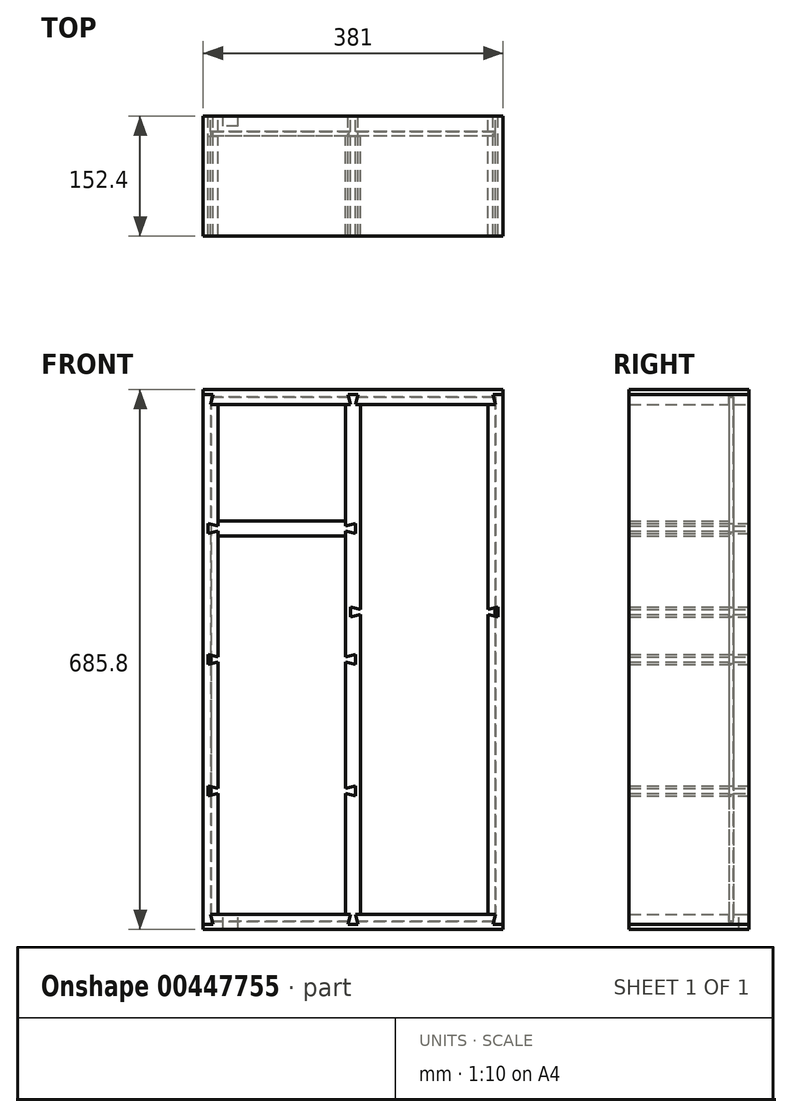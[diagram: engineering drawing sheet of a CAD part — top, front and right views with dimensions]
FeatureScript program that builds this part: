
annotation { "Feature Type Name" : "Feature", "Feature Type Description" : "" }
export const myFeature = defineFeature(function(context is Context, id is Id, definition is map)
    precondition{}
    {
        {
            var Q0;
            Q0=qCreatedBy(makeId("Front.planeOp"),FACE);
            var sketch = newSketch(context, id + "F0", { "sketchPlane" : qUnion([Q0])});
            skLineSegment(sketch, "E0.bottom", {"start": v(190.5, 342.9) * mm, "end": v(-190.5, 342.9) * mm});
            skLineSegment(sketch, "E0.top", {"start": v(190.5, -342.9) * mm, "end": v(-190.5, -342.9) * mm});
            skLineSegment(sketch, "E0.left", {"start": v(190.5, 342.9) * mm, "end": v(190.5, -342.9) * mm});
            skLineSegment(sketch, "E0.right", {"start": v(-190.5, 342.9) * mm, "end": v(-190.5, -342.9) * mm});
            skPoint(sketch, "E0.middle", {"position": v(0, 0) * mm});
            skLineSegment(sketch, "E1.0", {"start": v(-171.45, 323.85) * mm, "end": v(-171.45, -323.85) * mm});
            skLineSegment(sketch, "E1.1", {"start": v(190.5, 323.85) * mm, "end": v(-190.5, 323.85) * mm});
            skLineSegment(sketch, "E1.2", {"start": v(171.45, 323.85) * mm, "end": v(171.45, -323.85) * mm});
            skLineSegment(sketch, "E1.3", {"start": v(190.5, -323.85) * mm, "end": v(-190.5, -323.85) * mm});
            skLineSegment(sketch, "E2.0", {"start": v(171.45, 69.85) * mm, "end": v(9.53, 69.85) * mm});
            skLineSegment(sketch, "E3.0", {"start": v(171.45, 50.8) * mm, "end": v(9.53, 50.8) * mm});
            skLineSegment(sketch, "E4.0", {"start": v(-9.52, 323.85) * mm, "end": v(-9.52, 176.21) * mm});
            skLineSegment(sketch, "E5.0", {"start": v(9.53, 323.85) * mm, "end": v(9.52, -342.9) * mm});
            skLineSegment(sketch, "E6", {"start": v(-9.52, 176.21) * mm, "end": v(-9.53, -342.9) * mm});
            skLineSegment(sketch, "E7", {"start": v(-9.52, 157.16) * mm, "end": v(-171.45, 157.16) * mm});
            skLineSegment(sketch, "E8", {"start": v(-9.52, 176.21) * mm, "end": v(-171.45, 176.21) * mm});
            skLineSegment(sketch, "E9.direction1", {"start": v(-171.45, 157.16) * mm, "end": v(-146.05, 157.16) * mm, "construction": true});
            skLineSegment(sketch, "E9.direction2", {"start": v(-171.45, 157.16) * mm, "end": v(-171.45, -19.05) * mm, "construction": true});
            skLineSegment(sketch, "E10", {"start": v(-184.15, 173.04) * mm, "end": v(-184.15, 160.34) * mm});
            skLineSegment(sketch, "E11", {"start": v(-184.15, 160.34) * mm, "end": v(-171.45, 163.5) * mm});
            skLineSegment(sketch, "E12", {"start": v(-90.49, 176.21) * mm, "end": v(-90.49, 157.16) * mm, "construction": true});
            skLineSegment(sketch, "E13", {"start": v(-90.49, 157.16) * mm, "end": v(-90.49, 166.69) * mm, "construction": true});
            skLineSegment(sketch, "E14", {"start": v(-90.49, 166.69) * mm, "end": v(-171.45, 166.69) * mm, "construction": true});
            skLineSegment(sketch, "E15.MirrorCS", {"start": v(-90.49, 157.16) * mm, "end": v(-90.49, 176.21) * mm, "construction": true});
            skLineSegment(sketch, "E16.MirrorCS", {"start": v(-90.49, 176.21) * mm, "end": v(-90.49, 166.69) * mm, "construction": true});
            skLineSegment(sketch, "E17.MirrorCS", {"start": v(-184.15, 173.04) * mm, "end": v(-171.45, 169.87) * mm});
            skLineSegment(sketch, "E18.MirrorCS", {"start": v(3.18, 173.04) * mm, "end": v(-9.52, 169.87) * mm});
            skLineSegment(sketch, "E19.MirrorCS", {"start": v(3.18, 173.04) * mm, "end": v(3.18, 160.34) * mm});
            skLineSegment(sketch, "E20.MirrorCS", {"start": v(3.18, 160.34) * mm, "end": v(-9.52, 163.5) * mm});
            skLineSegment(sketch, "E21.0.1.0", {"start": v(-9.52, 9.53) * mm, "end": v(-171.45, 9.53) * mm});
            skLineSegment(sketch, "E21.0.1.1", {"start": v(-9.52, -9.53) * mm, "end": v(-171.45, -9.52) * mm});
            skLineSegment(sketch, "E21.0.1.2", {"start": v(3.18, 6.35) * mm, "end": v(-9.52, 3.18) * mm});
            skLineSegment(sketch, "E21.0.1.3", {"start": v(3.18, 6.35) * mm, "end": v(3.18, -6.35) * mm});
            skLineSegment(sketch, "E21.0.1.4", {"start": v(3.18, -6.35) * mm, "end": v(-9.52, -3.18) * mm});
            skLineSegment(sketch, "E21.0.1.5", {"start": v(-184.15, 6.35) * mm, "end": v(-171.45, 3.18) * mm});
            skLineSegment(sketch, "E21.0.1.6", {"start": v(-184.15, 6.35) * mm, "end": v(-184.15, -6.35) * mm});
            skLineSegment(sketch, "E21.0.1.7", {"start": v(-184.15, -6.35) * mm, "end": v(-171.45, -3.18) * mm});
            skLineSegment(sketch, "E21.0.2.0", {"start": v(-9.52, -157.16) * mm, "end": v(-171.45, -157.16) * mm});
            skLineSegment(sketch, "E21.0.2.1", {"start": v(-9.52, -176.21) * mm, "end": v(-171.45, -176.21) * mm});
            skLineSegment(sketch, "E21.0.2.2", {"start": v(3.18, -160.34) * mm, "end": v(-9.52, -163.5) * mm});
            skLineSegment(sketch, "E21.0.2.3", {"start": v(3.18, -160.34) * mm, "end": v(3.18, -173.04) * mm});
            skLineSegment(sketch, "E21.0.2.4", {"start": v(3.18, -173.04) * mm, "end": v(-9.52, -169.87) * mm});
            skLineSegment(sketch, "E21.0.2.5", {"start": v(-184.15, -160.34) * mm, "end": v(-171.45, -163.5) * mm});
            skLineSegment(sketch, "E21.0.2.6", {"start": v(-184.15, -160.34) * mm, "end": v(-184.15, -173.04) * mm});
            skLineSegment(sketch, "E21.0.2.7", {"start": v(-184.15, -173.04) * mm, "end": v(-171.45, -169.87) * mm});
            skLineSegment(sketch, "E21.direction1", {"start": v(-171.45, 176.21) * mm, "end": v(-146.05, 176.21) * mm, "construction": true});
            skLineSegment(sketch, "E21.direction2", {"start": v(-171.45, 176.21) * mm, "end": v(-171.45, 9.53) * mm, "construction": true});
            skLineSegment(sketch, "E22", {"start": v(90.49, 69.85) * mm, "end": v(90.49, 50.8) * mm, "construction": true});
            skLineSegment(sketch, "E23", {"start": v(90.49, 50.8) * mm, "end": v(90.49, 60.33) * mm, "construction": true});
            skLineSegment(sketch, "E24", {"start": v(90.49, 60.33) * mm, "end": v(9.53, 60.33) * mm, "construction": true});
            skLineSegment(sketch, "E25", {"start": v(-3.17, 66.68) * mm, "end": v(-3.17, 53.98) * mm});
            skLineSegment(sketch, "E26", {"start": v(-3.17, 53.98) * mm, "end": v(9.53, 57.14) * mm});
            skLineSegment(sketch, "E27.MirrorCS", {"start": v(-3.17, 66.68) * mm, "end": v(9.53, 63.5) * mm});
            skLineSegment(sketch, "E28.MirrorCS", {"start": v(184.15, 53.97) * mm, "end": v(171.45, 57.14) * mm});
            skLineSegment(sketch, "E29.MirrorCS", {"start": v(184.15, 66.67) * mm, "end": v(184.15, 53.98) * mm});
            skLineSegment(sketch, "E30.MirrorCS", {"start": v(184.15, 66.68) * mm, "end": v(171.45, 63.5) * mm});
            skLineSegment(sketch, "E31", {"start": v(-3.18, 323.85) * mm, "end": v(-6.35, 336.55) * mm});
            skLineSegment(sketch, "E32", {"start": v(-6.35, 336.55) * mm, "end": v(6.35, 336.55) * mm});
            skLineSegment(sketch, "E33", {"start": v(6.35, 336.55) * mm, "end": v(3.18, 323.85) * mm});
            skLineSegment(sketch, "E34", {"start": v(190.5, 0) * mm, "end": v(137.2, 0) * mm, "construction": true});
            skPoint(sketch, "E34.endSnap0", {"position": v(171.45, 0) * mm});
            skLineSegment(sketch, "E35.MirrorCS", {"start": v(-3.18, -323.85) * mm, "end": v(-6.35, -336.55) * mm});
            skLineSegment(sketch, "E36.MirrorCS", {"start": v(-6.35, -336.55) * mm, "end": v(6.35, -336.55) * mm});
            skLineSegment(sketch, "E37.MirrorCS", {"start": v(6.35, -336.55) * mm, "end": v(3.18, -323.85) * mm});
            skLineSegment(sketch, "E38.direction1", {"start": v(-3.18, 323.85) * mm, "end": v(-184.95, 323.85) * mm, "construction": true});
            skLineSegment(sketch, "E39", {"start": v(-190.5, 336.55) * mm, "end": v(-177.8, 336.55) * mm});
            skLineSegment(sketch, "E40", {"start": v(-177.8, 336.55) * mm, "end": v(-180.97, 323.85) * mm});
            skLineSegment(sketch, "E41", {"start": v(0, 336.55) * mm, "end": v(0, 342.9) * mm, "construction": true});
            skLineSegment(sketch, "E42.MirrorCS", {"start": v(190.5, 336.55) * mm, "end": v(177.8, 336.55) * mm});
            skLineSegment(sketch, "E43.MirrorCS", {"start": v(177.8, 336.55) * mm, "end": v(180.97, 323.85) * mm});
            skLineSegment(sketch, "E44.MirrorCS", {"start": v(-177.8, -336.55) * mm, "end": v(-180.97, -323.85) * mm});
            skLineSegment(sketch, "E45.MirrorCS", {"start": v(-190.5, -336.55) * mm, "end": v(-177.8, -336.55) * mm});
            skLineSegment(sketch, "E46.MirrorCS", {"start": v(190.5, -336.55) * mm, "end": v(177.8, -336.55) * mm});
            skLineSegment(sketch, "E47.MirrorCS", {"start": v(177.8, -336.55) * mm, "end": v(180.97, -323.85) * mm});
            skSolve(sketch);
        }
        {
            var Q0;
            Q0=makeQuery(id+"F0.imprint","IMPRINT",FACE,{"disambiguationData":[TD([[makeQuery(id+"F0.imprint","IMPRINT",EDGE,{"derivedFrom":sQuery(id+"F0.wireOp",EDGE,"E10")}),-1.0]])]});
            var Q1;
            Q1=makeQuery(id+"F0.imprint","IMPRINT",FACE,{"disambiguationData":[TD([[makeQuery(id+"F0.imprint","IMPRINT",EDGE,{"derivedFrom":sQuery(id+"F0.wireOp",EDGE,"E38.1.0.0")}),-1.0]])]});
            var Q2;
            {var subQ0=sQuery(id+"F0.wireOp",EDGE,"d3f680f3-c2c0-4e0c-b022-0988051007730.MirrorCS");Q2=makeQuery(id+"F0.imprint","IMPRINT",FACE,{"disambiguationData":[TD([[makeQuery(id+"F0.imprint","IMPRINT",EDGE,{"derivedFrom":subQ0}),1.0]])]});}
            var Q3;
            Q3=makeQuery(id+"F0.imprint","IMPRINT",FACE,{"disambiguationData":[TD([[makeQuery(id+"F0.imprint","IMPRINT",EDGE,{"derivedFrom":sQuery(id+"F0.wireOp",EDGE,"2740ed55-8f11-438f-acbb-cafe4e36e0a60.MirrorCS")}),1.0]])]});
            var Q4;
            {var subQ7=sQuery(id+"F0.wireOp",EDGE,"E28.MirrorCS");Q4=makeQuery(id+"F0.imprint","IMPRINT",FACE,{"disambiguationData":[TD([[makeQuery(id+"F0.imprint","IMPRINT",EDGE,{"derivedFrom":subQ7}),1.0]])]});}
            var Q5;
            {var subQ0=sQuery(id+"F0.wireOp",EDGE,"e1dd7cb1-112f-4285-ae75-c35135d77c9e0.MirrorCS");Q5=makeQuery(id+"F0.imprint","IMPRINT",FACE,{"disambiguationData":[TD([[makeQuery(id+"F0.imprint","IMPRINT",EDGE,{"derivedFrom":subQ0}),-1.0]])]});}
            var Q6;
            {var subQ3=sQuery(id+"F0.wireOp",EDGE,"E39");Q6=makeQuery(id+"F0.imprint","IMPRINT",FACE,{"disambiguationData":[TD([[makeQuery(id+"F0.imprint","IMPRINT",EDGE,{"derivedFrom":subQ3}),-1.0]])]});}
            var Q7;
            {var subQ4=sQuery(id+"F0.wireOp",EDGE,"E44.MirrorCS");Q7=makeQuery(id+"F0.imprint","IMPRINT",FACE,{"disambiguationData":[TD([[makeQuery(id+"F0.imprint","IMPRINT",EDGE,{"derivedFrom":subQ4}),1.0]])]});}
            var Q8;
            {var subQ3=sQuery(id+"F0.wireOp",EDGE,"E46.MirrorCS");Q8=makeQuery(id+"F0.imprint","IMPRINT",FACE,{"disambiguationData":[TD([[makeQuery(id+"F0.imprint","IMPRINT",EDGE,{"derivedFrom":subQ3}),-1.0]])]});}
            var Q9;
            {var subQ3=sQuery(id+"F0.wireOp",EDGE,"E42.MirrorCS");Q9=makeQuery(id+"F0.imprint","IMPRINT",FACE,{"disambiguationData":[TD([[makeQuery(id+"F0.imprint","IMPRINT",EDGE,{"derivedFrom":subQ3}),1.0]])]});}
            extrude(context, id + "F1", {"entities" : qUnion([Q0, Q1, Q2, Q3, Q4, Q5, Q6, Q7, Q8, Q9]), "depth" : 152.4 * mm});
        }
        {
            var Q0;
            Q0=makeQuery(id+"F0.imprint","IMPRINT",FACE,{"disambiguationData":[TD([[makeQuery(id+"F0.imprint","IMPRINT",EDGE,{"derivedFrom":sQuery(id+"F0.wireOp",EDGE,"E0.bottom")}),1.0]])]});
            var Q1;
            Q1=makeQuery(id+"F0.imprint","IMPRINT",FACE,{"disambiguationData":[TD([[makeQuery(id+"F0.imprint","IMPRINT",EDGE,{"derivedFrom":sQuery(id+"F0.wireOp",EDGE,"E0.top")}),-1.0]])]});
            var Q2;
            {var subQ5=sQuery(id+"F0.wireOp",EDGE,"E35.MirrorCS");Q2=makeQuery(id+"F0.imprint","IMPRINT",FACE,{"disambiguationData":[TD([[makeQuery(id+"F0.imprint","IMPRINT",EDGE,{"derivedFrom":subQ5}),-1.0]])]});}
            var Q3;
            Q3=makeQuery(id+"F1.opExtrude","CAP_FACE",FACE,{"disambiguationData":[OSD([sQuery(id+"F0.wireOp",EDGE,"E0.right"),sQuery(id+"F0.wireOp",EDGE,"E1.0"),sQuery(id+"F0.wireOp",EDGE,"6gt8yWgh-abrn-Wgjv-Y781-DDCKXzh4iFdJ"),sQuery(id+"F0.wireOp",EDGE,"8TpNQFgE-JifX-ycQU-W9cH-YHv9N8uHwDKs")])],"isStart":false});
            extrude(context, id + "F2", {"entities" : qUnion([Q0, Q1, Q2]), "endBound" : BoundingType.UP_TO_SURFACE, "endBoundEntityFace" : qUnion([Q3]), "depth" : 25.4 * mm});
        }
        {
            var Q0;
            Q0=makeQuery(id+"F2.opExtrude","CAP_FACE",FACE,{"disambiguationData":[OSD([sQuery(id+"F0.wireOp",EDGE,"E0.top"),sQuery(id+"F0.wireOp",EDGE,"E0.left"),sQuery(id+"F0.wireOp",EDGE,"E0.right"),sQuery(id+"F0.wireOp",EDGE,"E1.3"),sQuery(id+"F0.wireOp",EDGE,"E35.MirrorCS"),sQuery(id+"F0.wireOp",EDGE,"E36.MirrorCS"),sQuery(id+"F0.wireOp",EDGE,"E37.MirrorCS"),sQuery(id+"F0.wireOp",EDGE,"e1dd7cb1-112f-4285-ae75-c35135d77c9e0.MirrorCS"),sQuery(id+"F0.wireOp",EDGE,"44526457-2c17-440b-88b3-c98be03f3abe0.MirrorCS"),sQuery(id+"F0.wireOp",EDGE,"a112406e-55e0-4efe-a4f3-187d3dae983e0.MirrorCS"),sQuery(id+"F0.wireOp",EDGE,"d3f680f3-c2c0-4e0c-b022-0988051007730.MirrorCS"),sQuery(id+"F0.wireOp",EDGE,"5e166090-16c8-47ba-a701-47e76668f82e0.MirrorCS"),sQuery(id+"F0.wireOp",EDGE,"125f7c6a-878c-4f45-968d-a052c7d0f7940.MirrorCS")])],"isStart":true});
            var sketch = newSketch(context, id + "F3", { "sketchPlane" : qUnion([Q0])});
            skLineSegment(sketch, "E48.bottom", {"start": v(165.1, -342.9) * mm, "end": v(146.05, -342.9) * mm});
            skLineSegment(sketch, "E48.top", {"start": v(165.1, -323.85) * mm, "end": v(146.05, -323.85) * mm});
            skLineSegment(sketch, "E48.left", {"start": v(165.1, -342.9) * mm, "end": v(165.1, -323.85) * mm});
            skLineSegment(sketch, "E48.right", {"start": v(146.05, -342.9) * mm, "end": v(146.05, -323.85) * mm});
            skSolve(sketch);
        }
        {
            var Q0;
            Q0 = qSketchRegion(id + "F3", true);
            extrude(context, id + "F4", {"entities" : qUnion([Q0]), "operationType" : NewBodyOperationType.REMOVE, "oppositeDirection" : true, "depth" : 12.7 * mm});
        }
        {
            var Q0;
            Q0=qCreatedBy(makeId("Front.planeOp"),FACE);
            cPlane(context, id + "F5", {"entities" : qUnion([Q0]), "cplaneType" : CPlaneType.OFFSET, "offset" : 25.4 * mm, "width" : 152.4 * mm, "height" : 152.4 * mm});
        }
        {
            var Q0;
            Q0=qCreatedBy(id+"F5.planeOp",FACE);
            var sketch = newSketch(context, id + "F6", { "sketchPlane" : qUnion([Q0])});
            skLineSegment(sketch, "E49.0", {"start": v(-180.98, 333.38) * mm, "end": v(-180.97, -333.38) * mm});
            skLineSegment(sketch, "E49.1", {"start": v(180.97, 333.38) * mm, "end": v(-180.98, 333.38) * mm});
            skLineSegment(sketch, "E49.2", {"start": v(180.97, 333.38) * mm, "end": v(180.98, -333.38) * mm});
            skLineSegment(sketch, "E49.3", {"start": v(180.98, -333.38) * mm, "end": v(-180.97, -333.38) * mm});
            skSolve(sketch);
        }
        {
            var Q0;
            Q0 = qSketchRegion(id + "F6", true);
            extrude(context, id + "F7", {"entities" : qUnion([Q0]), "operationType" : NewBodyOperationType.REMOVE, "oppositeDirection" : true, "depth" : 5.56 * mm});
        }
        {
            var Q0;
            Q0=qCreatedBy(id+"F5.planeOp",FACE);
            var sketch = newSketch(context, id + "F8", { "sketchPlane" : qUnion([Q0])});
            skLineSegment(sketch, "E50.0", {"start": v(-180.18, 332.58) * mm, "end": v(-180.18, -332.58) * mm});
            skLineSegment(sketch, "E50.1", {"start": v(180.18, 332.58) * mm, "end": v(-180.18, 332.58) * mm});
            skLineSegment(sketch, "E50.2", {"start": v(180.18, 332.58) * mm, "end": v(180.18, -332.58) * mm});
            skLineSegment(sketch, "E50.3", {"start": v(180.18, -332.58) * mm, "end": v(-180.18, -332.58) * mm});
            skSolve(sketch);
        }
        {
            var Q0;
            Q0 = qSketchRegion(id + "F8", true);
            extrude(context, id + "F9", {"entities" : qUnion([Q0]), "oppositeDirection" : true, "depth" : 5 * mm});
        }
        {
            var Q0;
            Q0=makeQuery(id+"F9.opExtrude","CAP_FACE",FACE,{"disambiguationData":[OSD([sQuery(id+"F8.wireOp",EDGE,"E50.0"),sQuery(id+"F8.wireOp",EDGE,"E50.1"),sQuery(id+"F8.wireOp",EDGE,"E50.2"),sQuery(id+"F8.wireOp",EDGE,"E50.3")])],"isStart":true});
            var sketch = newSketch(context, id + "F10", { "sketchPlane" : qUnion([Q0])});
            skLineSegment(sketch, "E51.0", {"start": v(9.53, 323.85) * mm, "end": v(3.18, 323.85) * mm});
            skLineSegment(sketch, "E51.1", {"start": v(-3.18, 323.85) * mm, "end": v(-6.35, 336.55) * mm});
            skLineSegment(sketch, "E51.2", {"start": v(-6.35, 336.55) * mm, "end": v(6.35, 336.55) * mm});
            skLineSegment(sketch, "E51.3", {"start": v(6.35, 336.55) * mm, "end": v(3.18, 323.85) * mm});
            skLineSegment(sketch, "E51.4", {"start": v(9.53, 323.85) * mm, "end": v(9.53, 63.5) * mm});
            skLineSegment(sketch, "E51.5", {"start": v(3.18, 173.04) * mm, "end": v(-9.52, 169.87) * mm});
            skLineSegment(sketch, "E51.6", {"start": v(3.18, 173.04) * mm, "end": v(3.18, 160.34) * mm});
            skLineSegment(sketch, "E51.7", {"start": v(3.18, 160.34) * mm, "end": v(-9.52, 163.5) * mm});
            skLineSegment(sketch, "E51.9", {"start": v(-9.52, 323.85) * mm, "end": v(-9.52, 169.87) * mm});
            skLineSegment(sketch, "E51.10", {"start": v(3.18, -160.34) * mm, "end": v(3.18, -173.04) * mm});
            skLineSegment(sketch, "E51.11", {"start": v(3.18, -173.04) * mm, "end": v(-9.52, -169.87) * mm});
            skLineSegment(sketch, "E51.12", {"start": v(3.18, -160.34) * mm, "end": v(-9.52, -163.5) * mm});
            skLineSegment(sketch, "E51.13", {"start": v(9.52, -323.85) * mm, "end": v(3.18, -323.85) * mm});
            skLineSegment(sketch, "E51.14", {"start": v(-3.18, -323.85) * mm, "end": v(-6.35, -336.55) * mm});
            skLineSegment(sketch, "E51.15", {"start": v(-6.35, -336.55) * mm, "end": v(6.35, -336.55) * mm});
            skLineSegment(sketch, "E51.16", {"start": v(6.35, -336.55) * mm, "end": v(3.18, -323.85) * mm});
            skPoint(sketch, "E52.orphan", {"position": v(-190.5, -323.85) * mm});
            skPoint(sketch, "E53.orphan", {"position": v(190.5, -323.85) * mm});
            skLineSegment(sketch, "E54.trimOffspring", {"start": v(-9.52, -169.87) * mm, "end": v(-9.52, -323.85) * mm});
            skLineSegment(sketch, "E55.trimOffspring", {"start": v(-9.53, 163.5) * mm, "end": v(-9.52, -163.5) * mm});
            skPoint(sketch, "E51.8.start.orphan", {"position": v(-9.52, 176.21) * mm});
            skPoint(sketch, "E56.orphan", {"position": v(190.5, 323.85) * mm});
            skPoint(sketch, "E57.orphan", {"position": v(-190.5, 323.85) * mm});
            skLineSegment(sketch, "E58.trimOffspring", {"start": v(-3.18, 323.85) * mm, "end": v(-9.52, 323.85) * mm});
            skLineSegment(sketch, "E59.0", {"start": v(-3.17, 66.68) * mm, "end": v(9.53, 63.5) * mm});
            skLineSegment(sketch, "E59.1", {"start": v(-3.17, 66.68) * mm, "end": v(-3.17, 53.98) * mm});
            skLineSegment(sketch, "E59.2", {"start": v(-3.17, 53.98) * mm, "end": v(9.53, 57.14) * mm});
            skLineSegment(sketch, "E60.trimOffspring", {"start": v(9.52, 57.14) * mm, "end": v(9.53, -323.85) * mm});
            skLineSegment(sketch, "E61.0", {"start": v(3.18, 6.35) * mm, "end": v(-9.53, 3.18) * mm});
            skLineSegment(sketch, "E61.1", {"start": v(3.18, 6.35) * mm, "end": v(3.18, -6.35) * mm});
            skLineSegment(sketch, "E61.2", {"start": v(3.18, -6.35) * mm, "end": v(-9.53, -3.18) * mm});
            skPoint(sketch, "E62.orphan", {"position": v(9.52, -342.9) * mm});
            skLineSegment(sketch, "E63.0", {"start": v(-3.18, -323.85) * mm, "end": v(-9.53, -323.85) * mm});
            skPoint(sketch, "E64.orphan", {"position": v(-180.97, -323.85) * mm});
            skPoint(sketch, "E65.orphan", {"position": v(-9.53, -342.9) * mm});
            skSolve(sketch);
        }
        {
            var Q0;
            {var subQ0=sQuery(id+"F10.wireOp",EDGE,"E51.2");Q0=makeQuery(id+"F10.imprint","IMPRINT",FACE,{"disambiguationData":[TD([[makeQuery(id+"F10.imprint","IMPRINT",EDGE,{"derivedFrom":subQ0}),-1.0]])]});}
            var Q1;
            {var subQ0=sQuery(id+"F10.wireOp",EDGE,"E51.15");Q1=makeQuery(id+"F10.imprint","IMPRINT",FACE,{"disambiguationData":[TD([[makeQuery(id+"F10.imprint","IMPRINT",EDGE,{"derivedFrom":subQ0}),1.0]])]});}
            var Q2;
            {var subQ17=sQuery(id+"F10.wireOp",EDGE,"E51.0");Q2=makeQuery(id+"F10.imprint","IMPRINT",FACE,{"disambiguationData":[TD([[makeQuery(id+"F10.imprint","IMPRINT",EDGE,{"derivedFrom":subQ17}),1.0]])]});}
            var Q3;
            Q3=makeQuery(id+"F1.opExtrude","CAP_FACE",FACE,{"disambiguationData":[OSD([sQuery(id+"F0.wireOp",EDGE,"E0.right"),sQuery(id+"F0.wireOp",EDGE,"E1.0"),sQuery(id+"F0.wireOp",EDGE,"6gt8yWgh-abrn-Wgjv-Y781-DDCKXzh4iFdJ"),sQuery(id+"F0.wireOp",EDGE,"8TpNQFgE-JifX-ycQU-W9cH-YHv9N8uHwDKs"),sQuery(id+"F0.wireOp",EDGE,"E10"),sQuery(id+"F0.wireOp",EDGE,"E11"),sQuery(id+"F0.wireOp",EDGE,"E17.MirrorCS"),sQuery(id+"F0.wireOp",EDGE,"E21.0.1.5"),sQuery(id+"F0.wireOp",EDGE,"E21.0.1.6"),sQuery(id+"F0.wireOp",EDGE,"E21.0.1.7"),sQuery(id+"F0.wireOp",EDGE,"E21.0.2.5"),sQuery(id+"F0.wireOp",EDGE,"E21.0.2.6"),sQuery(id+"F0.wireOp",EDGE,"E21.0.2.7")])],"isStart":false});
            extrude(context, id + "F11", {"entities" : qUnion([Q0, Q1, Q2]), "endBound" : BoundingType.UP_TO_SURFACE, "endBoundEntityFace" : qUnion([Q3]), "depth" : 25.4 * mm});
        }
        {
            var Q0;
            Q0=makeQuery(id+"F9.opExtrude","CAP_FACE",FACE,{"disambiguationData":[OSD([sQuery(id+"F8.wireOp",EDGE,"E50.0"),sQuery(id+"F8.wireOp",EDGE,"E50.1"),sQuery(id+"F8.wireOp",EDGE,"E50.2"),sQuery(id+"F8.wireOp",EDGE,"E50.3")])],"isStart":true});
            var sketch = newSketch(context, id + "F12", { "sketchPlane" : qUnion([Q0])});
            skLineSegment(sketch, "E66.0", {"start": v(-9.52, 176.21) * mm, "end": v(-171.45, 176.21) * mm});
            skLineSegment(sketch, "E66.1", {"start": v(-171.45, 323.85) * mm, "end": v(-171.45, 169.87) * mm});
            skLineSegment(sketch, "E66.2", {"start": v(-184.15, 173.04) * mm, "end": v(-171.45, 169.87) * mm});
            skLineSegment(sketch, "E66.3", {"start": v(-184.15, 173.04) * mm, "end": v(-184.15, 160.34) * mm});
            skLineSegment(sketch, "E66.4", {"start": v(-184.15, 160.34) * mm, "end": v(-171.45, 163.5) * mm});
            skLineSegment(sketch, "E66.5", {"start": v(-9.52, 157.16) * mm, "end": v(-171.45, 157.16) * mm});
            skLineSegment(sketch, "E66.6", {"start": v(3.18, 173.04) * mm, "end": v(-9.52, 169.87) * mm});
            skLineSegment(sketch, "E66.7", {"start": v(3.18, 173.04) * mm, "end": v(3.18, 160.34) * mm});
            skLineSegment(sketch, "E66.8", {"start": v(3.18, 160.34) * mm, "end": v(-9.52, 163.5) * mm});
            skLineSegment(sketch, "E66.9", {"start": v(-9.52, 176.21) * mm, "end": v(-9.52, 169.87) * mm});
            skPoint(sketch, "E67.orphan", {"position": v(-9.53, -342.9) * mm});
            skLineSegment(sketch, "E68.trimOffspring", {"start": v(-9.53, 163.5) * mm, "end": v(-9.53, 157.16) * mm});
            skPoint(sketch, "E69.orphan", {"position": v(-171.45, -323.85) * mm});
            skLineSegment(sketch, "E70.trimOffspring", {"start": v(-171.45, 163.5) * mm, "end": v(-171.45, 157.16) * mm});
            skSolve(sketch);
        }
        {
            var Q0;
            Q0 = qSketchRegion(id + "F12", true);
            var Q1;
            Q1=makeQuery(id+"F1.opExtrude","CAP_FACE",FACE,{"disambiguationData":[OSD([sQuery(id+"F0.wireOp",EDGE,"E0.right"),sQuery(id+"F0.wireOp",EDGE,"E1.0"),sQuery(id+"F0.wireOp",EDGE,"6gt8yWgh-abrn-Wgjv-Y781-DDCKXzh4iFdJ"),sQuery(id+"F0.wireOp",EDGE,"8TpNQFgE-JifX-ycQU-W9cH-YHv9N8uHwDKs"),sQuery(id+"F0.wireOp",EDGE,"E10"),sQuery(id+"F0.wireOp",EDGE,"E11"),sQuery(id+"F0.wireOp",EDGE,"E17.MirrorCS"),sQuery(id+"F0.wireOp",EDGE,"E21.0.1.5"),sQuery(id+"F0.wireOp",EDGE,"E21.0.1.6"),sQuery(id+"F0.wireOp",EDGE,"E21.0.1.7"),sQuery(id+"F0.wireOp",EDGE,"E21.0.2.5"),sQuery(id+"F0.wireOp",EDGE,"E21.0.2.6"),sQuery(id+"F0.wireOp",EDGE,"E21.0.2.7")])],"isStart":false});
            extrude(context, id + "F13", {"entities" : qUnion([Q0]), "endBound" : BoundingType.UP_TO_SURFACE, "endBoundEntityFace" : qUnion([Q1]), "depth" : 25.4 * mm});
        }
    });
